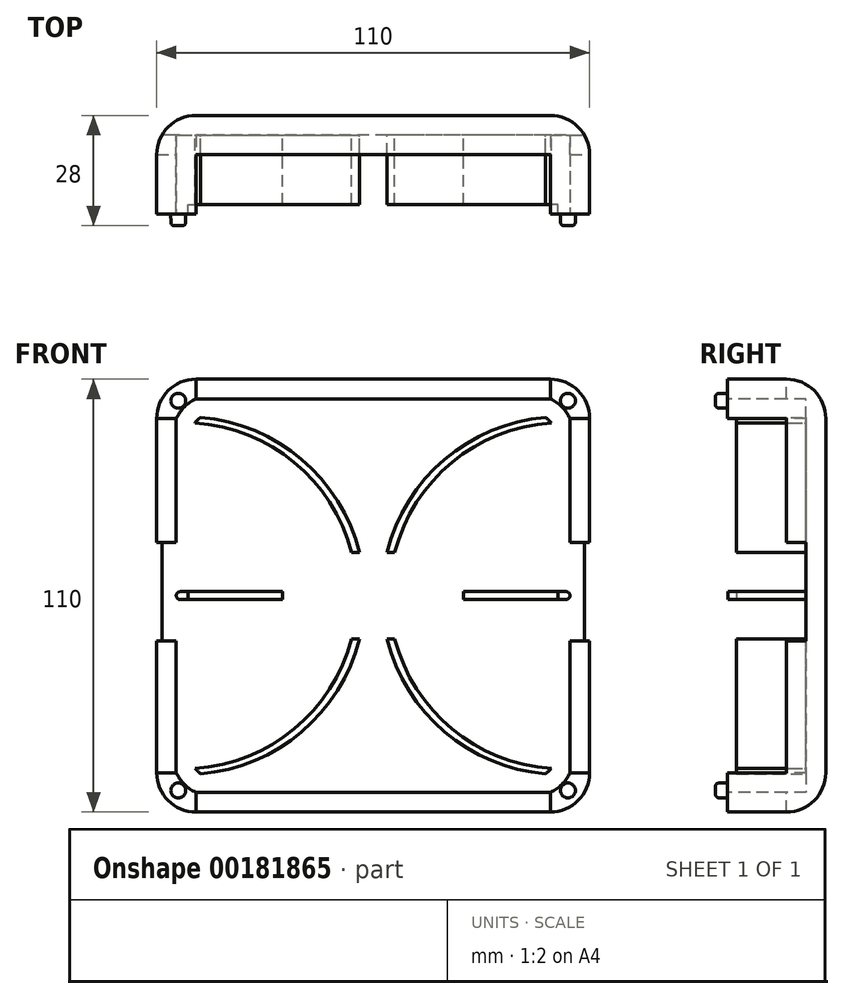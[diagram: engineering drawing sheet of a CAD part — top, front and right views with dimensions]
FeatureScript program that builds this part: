
annotation { "Feature Type Name" : "Feature", "Feature Type Description" : "" }
export const myFeature = defineFeature(function(context is Context, id is Id, definition is map)
    precondition{}
    {
        {
            var Q0;
            Q0=qCreatedBy(makeId("Front.planeOp"),FACE);
            var sketch = newSketch(context, id + "F0", { "sketchPlane" : qUnion([Q0])});
            skLineSegment(sketch, "E0.bottom", {"start": v(-55, 55) * mm, "end": v(55, 55) * mm});
            skLineSegment(sketch, "E0.top", {"start": v(-55, -55) * mm, "end": v(55, -55) * mm});
            skLineSegment(sketch, "E0.left", {"start": v(-55, 55) * mm, "end": v(-55, -55) * mm});
            skLineSegment(sketch, "E0.right", {"start": v(55, 55) * mm, "end": v(55, -55) * mm});
            skPoint(sketch, "E1", {"position": v(0, 55) * mm});
            skPoint(sketch, "E2", {"position": v(-55, 0) * mm});
            skPoint(sketch, "E3", {"position": v(55, 0) * mm});
            skPoint(sketch, "E4", {"position": v(0, -55) * mm});
            skSolve(sketch);
        }
        {
            var Q0;
            Q0=qSketchRegion(id+"F0",true);
            extrude(context, id + "F1", {"entities" : qUnion([Q0]), "endBound" : BoundingType.SYMMETRIC, "depth" : 50 * mm});
        }
        {
            var Q0;
            Q0=makeQuery(id+"F1.opExtrude","CAP_FACE",FACE,{"disambiguationData":[OSD([sQuery(id+"F0.wireOp",EDGE,"E0.bottom"),sQuery(id+"F0.wireOp",EDGE,"E0.top"),sQuery(id+"F0.wireOp",EDGE,"E0.left"),sQuery(id+"F0.wireOp",EDGE,"E0.right")])],"isStart":false});
            var Q1;
            Q1=makeQuery(id+"F1.opExtrude","SWEPT_FACE",FACE,{"disambiguationData":[OSD([sQuery(id+"F0.wireOp",EDGE,"E0.right")])]});
            var Q2;
            Q2=makeQuery(id+"F1.opExtrude","SWEPT_FACE",FACE,{"disambiguationData":[OSD([sQuery(id+"F0.wireOp",EDGE,"E0.bottom")])]});
            var Q3;
            Q3=makeQuery(id+"F1.opExtrude","SWEPT_FACE",FACE,{"disambiguationData":[OSD([sQuery(id+"F0.wireOp",EDGE,"E0.left")])]});
            var Q4;
            Q4=makeQuery(id+"F1.opExtrude","SWEPT_FACE",FACE,{"disambiguationData":[OSD([sQuery(id+"F0.wireOp",EDGE,"E0.top")])]});
            fillet(context, id + "F2", {"entities" : qUnion([Q0, Q1, Q2, Q3, Q4]), "radius" : 10 * mm, "allowEdgeOverflow" : false});
        }
        {
            var Q0;
            Q0=qCreatedBy(makeId("Front.planeOp"),FACE);
            var sketch = newSketch(context, id + "F3", { "sketchPlane" : qUnion([Q0])});
            skLineSegment(sketch, "E5.bottom", {"start": v(55, 55) * mm, "end": v(-55, 55) * mm});
            skLineSegment(sketch, "E5.top", {"start": v(55, -55) * mm, "end": v(-55, -55) * mm});
            skLineSegment(sketch, "E5.left", {"start": v(-55, 55) * mm, "end": v(-55, -55) * mm});
            skLineSegment(sketch, "E5.right", {"start": v(55, 55) * mm, "end": v(55, -55) * mm});
            skPoint(sketch, "E6", {"position": v(0, 55) * mm});
            skPoint(sketch, "E7", {"position": v(-55, 0) * mm});
            skPoint(sketch, "E8", {"position": v(55, 0) * mm});
            skPoint(sketch, "E9", {"position": v(0, -55) * mm});
            skSolve(sketch);
        }
        {
            var Q0;
            Q0=qSketchRegion(id+"F3",true);
            extrude(context, id + "F4", {"entities" : qUnion([Q0]), "operationType" : NewBodyOperationType.REMOVE, "depth" : 26 * mm});
        }
        {
            var Q0;
            Q0=qCreatedBy(makeId("Front.planeOp"),FACE);
            var sketch = newSketch(context, id + "F5", { "sketchPlane" : qUnion([Q0])});
            skLineSegment(sketch, "E10", {"start": v(45, 50) * mm, "end": v(-45, 50) * mm});
            skLineSegment(sketch, "E11", {"start": v(-45, 50) * mm, "end": v(-45, 45) * mm});
            skLineSegment(sketch, "E12", {"start": v(45, 50) * mm, "end": v(45, 45) * mm});
            skLineSegment(sketch, "E13", {"start": v(50, 45) * mm, "end": v(50, -45) * mm});
            skLineSegment(sketch, "E14", {"start": v(50, -45) * mm, "end": v(45, -45) * mm});
            skLineSegment(sketch, "E15", {"start": v(45, -45) * mm, "end": v(45, -50) * mm});
            skLineSegment(sketch, "E16", {"start": v(45, -50) * mm, "end": v(-45, -50) * mm});
            skLineSegment(sketch, "E17", {"start": v(-45, -50) * mm, "end": v(-45, -45) * mm});
            skLineSegment(sketch, "E18", {"start": v(-45, -45) * mm, "end": v(-50, -45) * mm});
            skLineSegment(sketch, "E19", {"start": v(-50, -45) * mm, "end": v(-50, 45) * mm});
            skLineSegment(sketch, "E20", {"start": v(-50, 45) * mm, "end": v(-45, 45) * mm});
            skLineSegment(sketch, "E21.MirrorCS", {"start": v(50, 45) * mm, "end": v(45, 45) * mm});
            skSolve(sketch);
        }
        {
            var Q0;
            Q0=qSketchRegion(id+"F5",true);
            extrude(context, id + "F6", {"entities" : qUnion([Q0]), "operationType" : NewBodyOperationType.REMOVE, "oppositeDirection" : true, "depth" : 20 * mm});
        }
        {
            var Q0;
            Q0=makeQuery(id+"F4.boolean.opBoolean","COPY",FACE,{"derivedFrom":makeQuery(id+"F4.opExtrude","CAP_FACE",FACE,{"disambiguationData":[OSD([sQuery(id+"F3.wireOp",EDGE,"E5.bottom"),sQuery(id+"F3.wireOp",EDGE,"E5.top"),sQuery(id+"F3.wireOp",EDGE,"E5.left"),sQuery(id+"F3.wireOp",EDGE,"E5.right")])],"isStart":true})});
            var sketch = newSketch(context, id + "F7", { "sketchPlane" : qUnion([Q0])});
            skCircle(sketch, "E22", {"center": v(49.5, 49.5) * mm, "radius": 1.9 * mm});
            skCircle(sketch, "E23.MirrorC", {"center": v(-49.5, 49.5) * mm, "radius": 1.9 * mm});
            skCircle(sketch, "E24.MirrorC", {"center": v(49.5, -49.5) * mm, "radius": 1.9 * mm});
            skCircle(sketch, "E25.MirrorC", {"center": v(-49.5, -49.5) * mm, "radius": 1.9 * mm});
            skSolve(sketch);
        }
        {
            var Q0;
            Q0=qSketchRegion(id+"F7",true);
            extrude(context, id + "F8", {"entities" : qUnion([Q0]), "operationType" : NewBodyOperationType.ADD, "depth" : 3 * mm, "hasDraft" : true, "draftAngle" : 1 * degree, "draftPullDirection" : true});
        }
        {
            var Q0;
            Q0=makeQuery(id+"F4.boolean.opBoolean","COPY",FACE,{"derivedFrom":makeQuery(id+"F4.opExtrude","CAP_FACE",FACE,{"disambiguationData":[OSD([sQuery(id+"F3.wireOp",EDGE,"E5.bottom"),sQuery(id+"F3.wireOp",EDGE,"E5.top"),sQuery(id+"F3.wireOp",EDGE,"E5.left"),sQuery(id+"F3.wireOp",EDGE,"E5.right")])],"isStart":true})});
            var sketch = newSketch(context, id + "F9", { "sketchPlane" : qUnion([Q0])});
            skArc(sketch, "E26", {"start": v(-45, 50) * mm, "mid": v(-47.96, 47.96) * mm, "end": v(-50, 45) * mm});
            skLineSegment(sketch, "E27", {"start": v(-45, 50) * mm, "end": v(-45, 45) * mm});
            skLineSegment(sketch, "E28", {"start": v(-45, 45) * mm, "end": v(-50, 45) * mm});
            skLineSegment(sketch, "E29.MirrorCS", {"start": v(-45, -50) * mm, "end": v(-45, -45) * mm});
            skArc(sketch, "E30.MirrorCS", {"start": v(-45, -50) * mm, "mid": v(-47.96, -47.96) * mm, "end": v(-50, -45) * mm});
            skLineSegment(sketch, "E31.MirrorCS", {"start": v(-45, -45) * mm, "end": v(-50, -45) * mm});
            skArc(sketch, "E32.MirrorCS", {"start": v(45, 50) * mm, "mid": v(47.96, 47.96) * mm, "end": v(50, 45) * mm});
            skLineSegment(sketch, "E33.MirrorCS", {"start": v(45, 50) * mm, "end": v(45, 45) * mm});
            skLineSegment(sketch, "E34.MirrorCS", {"start": v(45, 45) * mm, "end": v(50, 45) * mm});
            skLineSegment(sketch, "E35.MirrorCS", {"start": v(45, -45) * mm, "end": v(50, -45) * mm});
            skArc(sketch, "E36.MirrorCS", {"start": v(45, -50) * mm, "mid": v(47.96, -47.96) * mm, "end": v(50, -45) * mm});
            skLineSegment(sketch, "E37.MirrorCS", {"start": v(45, -50) * mm, "end": v(45, -45) * mm});
            skSolve(sketch);
        }
        {
            var Q0;
            Q0 = qSketchRegion(id + "F9", true);
            extrude(context, id + "F10", {"entities" : qUnion([Q0]), "operationType" : NewBodyOperationType.REMOVE, "oppositeDirection" : true, "depth" : 20 * mm});
        }
        {
            var Q0;
            Q0=makeQuery(id+"F1.opExtrude","SWEPT_FACE",FACE,{"disambiguationData":[OSD([sQuery(id+"F0.wireOp",EDGE,"E0.bottom")])]});
            var sketch = newSketch(context, id + "F11", { "sketchPlane" : qUnion([Q0])});
            skLineSegment(sketch, "E38.bottom", {"start": v(-45, 15) * mm, "end": v(45, 15) * mm});
            skLineSegment(sketch, "E38.top", {"start": v(-45, 0) * mm, "end": v(45, 0) * mm});
            skLineSegment(sketch, "E38.left", {"start": v(-45, 15) * mm, "end": v(-45, 0) * mm});
            skLineSegment(sketch, "E38.right", {"start": v(45, 15) * mm, "end": v(45, 0) * mm});
            skSolve(sketch);
        }
        {
            var Q0;
            Q0 = qSketchRegion(id + "F11", true);
            extrude(context, id + "F12", {"entities" : qUnion([Q0]), "operationType" : NewBodyOperationType.REMOVE, "oppositeDirection" : true, "depth" : 110 * mm});
        }
        {
            var Q0;
            Q0=makeQuery(id+"F1.opExtrude","SWEPT_FACE",FACE,{"disambiguationData":[OSD([sQuery(id+"F0.wireOp",EDGE,"E0.left")])]});
            var sketch = newSketch(context, id + "F13", { "sketchPlane" : qUnion([Q0])});
            skLineSegment(sketch, "E39.bottom", {"start": v(-15, -45) * mm, "end": v(0, -45) * mm});
            skLineSegment(sketch, "E39.top", {"start": v(-15, 45) * mm, "end": v(0, 45) * mm});
            skLineSegment(sketch, "E39.left", {"start": v(-15, -45) * mm, "end": v(-15, 45) * mm});
            skLineSegment(sketch, "E39.right", {"start": v(0, -45) * mm, "end": v(0, 45) * mm});
            skSolve(sketch);
        }
        {
            var Q0;
            Q0 = qSketchRegion(id + "F13", true);
            extrude(context, id + "F14", {"entities" : qUnion([Q0]), "operationType" : NewBodyOperationType.REMOVE, "oppositeDirection" : true, "depth" : 110 * mm});
        }
        {
            var Q0;
            Q0=makeQuery(id+"F10.boolean.opBoolean","MERGE",FACE,{"derivedFrom":[makeQuery(id+"F6.boolean.opBoolean","COPY",FACE,{"derivedFrom":makeQuery(id+"F6.opExtrude","CAP_FACE",FACE,{"disambiguationData":[OSD([sQuery(id+"F5.wireOp",EDGE,"E10"),sQuery(id+"F5.wireOp",EDGE,"E11"),sQuery(id+"F5.wireOp",EDGE,"E12"),sQuery(id+"F5.wireOp",EDGE,"Rgk4YyDA-dK0y-lxdy-LCG8-8X0n81pjpPL2"),sQuery(id+"F5.wireOp",EDGE,"E13"),sQuery(id+"F5.wireOp",EDGE,"E14"),sQuery(id+"F5.wireOp",EDGE,"E15"),sQuery(id+"F5.wireOp",EDGE,"E16"),sQuery(id+"F5.wireOp",EDGE,"E17"),sQuery(id+"F5.wireOp",EDGE,"E18"),sQuery(id+"F5.wireOp",EDGE,"E19"),sQuery(id+"F5.wireOp",EDGE,"E20")])],"isStart":false})}),makeQuery(id+"F10.opExtrude","CAP_FACE",FACE,{"disambiguationData":[OSD([sQuery(id+"F9.wireOp",EDGE,"E26"),sQuery(id+"F9.wireOp",EDGE,"E27"),sQuery(id+"F9.wireOp",EDGE,"E28")])],"isStart":false}),makeQuery(id+"F10.opExtrude","CAP_FACE",FACE,{"disambiguationData":[OSD([sQuery(id+"F9.wireOp",EDGE,"E29.MirrorCS"),sQuery(id+"F9.wireOp",EDGE,"E30.MirrorCS"),sQuery(id+"F9.wireOp",EDGE,"E31.MirrorCS")])],"isStart":false}),makeQuery(id+"F10.opExtrude","CAP_FACE",FACE,{"disambiguationData":[OSD([sQuery(id+"F9.wireOp",EDGE,"713af9eb-3523-4645-b4d6-e8278202f2d70.MirrorCS"),sQuery(id+"F9.wireOp",EDGE,"aa040882-3397-4691-b8a4-aef4612770bb0.MirrorCS"),sQuery(id+"F9.wireOp",EDGE,"7d541f15-c5d7-4458-aec9-df448ef9912d0.MirrorCS")])],"isStart":false}),makeQuery(id+"F10.opExtrude","CAP_FACE",FACE,{"disambiguationData":[OSD([sQuery(id+"F9.wireOp",EDGE,"zS62jr0F-Xqa5-w36F-4dhE-6Vk6gu5LrxYo"),sQuery(id+"F9.wireOp",EDGE,"QpDyHDuu-1PBp-T7AA-cmtf-nKKC5eDHPDcg"),sQuery(id+"F9.wireOp",EDGE,"hVT4Xi0K-uElt-0SsE-6UHd-I7Wh2zfzxc4D")])],"isStart":false})]});
            var sketch = newSketch(context, id + "F15", { "sketchPlane" : qUnion([Q0])});
            skLineSegment(sketch, "E40.bottom", {"start": v(-50, 1) * mm, "end": v(-23, 1) * mm});
            skLineSegment(sketch, "E40.top", {"start": v(-50, -1) * mm, "end": v(-23, -1) * mm});
            skLineSegment(sketch, "E40.left", {"start": v(-50, 1) * mm, "end": v(-50, -1) * mm});
            skLineSegment(sketch, "E40.right", {"start": v(-23, 1) * mm, "end": v(-23, -1) * mm});
            skPoint(sketch, "E41", {"position": v(-50, 0) * mm});
            skLineSegment(sketch, "E42.MirrorCS", {"start": v(50, 1) * mm, "end": v(23, 1) * mm});
            skLineSegment(sketch, "E43.MirrorCS", {"start": v(50, -1) * mm, "end": v(23, -1) * mm});
            skLineSegment(sketch, "E44.MirrorCS", {"start": v(23, 1) * mm, "end": v(23, -1) * mm});
            skLineSegment(sketch, "E45.MirrorCS", {"start": v(50, 1) * mm, "end": v(50, -1) * mm});
            skLineSegment(sketch, "E46.bottom", {"start": v(-23, 8) * mm, "end": v(23, 8) * mm});
            skLineSegment(sketch, "E46.top", {"start": v(-23, -8) * mm, "end": v(23, -8) * mm});
            skPoint(sketch, "E47", {"position": v(-23, 0) * mm});
            skPoint(sketch, "E48", {"position": v(0, 8) * mm});
            skPoint(sketch, "E49", {"position": v(-3.5, 8) * mm});
            skArc(sketch, "E50", {"start": v(-3.5, 11) * mm, "mid": v(-18.17, 34.62) * mm, "end": v(-43.85, 45.26) * mm});
            skPoint(sketch, "E51", {"position": v(-43.85, 45.26) * mm});
            skPoint(sketch, "E52", {"position": v(-45.26, 43.85) * mm});
            skPoint(sketch, "E53", {"position": v(-5.5, 8) * mm});
            skArc(sketch, "E54", {"start": v(-5.5, 11) * mm, "mid": v(-20.05, 33.87) * mm, "end": v(-45.26, 43.85) * mm});
            skLineSegment(sketch, "E55", {"start": v(-5.5, 11) * mm, "end": v(-3.5, 11) * mm});
            skArc(sketch, "E56", {"start": v(-43.85, 45.26) * mm, "mid": v(-44.6, 44.6) * mm, "end": v(-45.26, 43.85) * mm});
            skArc(sketch, "E57.MirrorCS", {"start": v(5.5, 11) * mm, "mid": v(20.05, 33.87) * mm, "end": v(45.26, 43.85) * mm});
            skArc(sketch, "E58.MirrorCS", {"start": v(3.5, 11) * mm, "mid": v(18.17, 34.62) * mm, "end": v(43.85, 45.26) * mm});
            skArc(sketch, "E59.MirrorCS", {"start": v(43.85, 45.26) * mm, "mid": v(44.6, 44.6) * mm, "end": v(45.26, 43.85) * mm});
            skLineSegment(sketch, "E60.MirrorCS", {"start": v(5.5, 11) * mm, "end": v(3.5, 11) * mm});
            skArc(sketch, "E61.MirrorCS", {"start": v(-5.5, -11) * mm, "mid": v(-20.05, -33.87) * mm, "end": v(-45.26, -43.85) * mm});
            skArc(sketch, "E62.MirrorCS", {"start": v(-3.5, -11) * mm, "mid": v(-18.17, -34.62) * mm, "end": v(-43.85, -45.26) * mm});
            skArc(sketch, "E63.MirrorCS", {"start": v(5.5, -11) * mm, "mid": v(20.05, -33.87) * mm, "end": v(45.26, -43.85) * mm});
            skArc(sketch, "E64.MirrorCS", {"start": v(3.5, -11) * mm, "mid": v(18.17, -34.62) * mm, "end": v(43.85, -45.26) * mm});
            skLineSegment(sketch, "E65.MirrorCS", {"start": v(-5.5, -11) * mm, "end": v(-3.5, -11) * mm});
            skLineSegment(sketch, "E66.MirrorCS", {"start": v(5.5, -11) * mm, "end": v(3.5, -11) * mm});
            skArc(sketch, "E67.MirrorCS", {"start": v(43.85, -45.26) * mm, "mid": v(44.6, -44.6) * mm, "end": v(45.26, -43.85) * mm});
            skArc(sketch, "E68.MirrorCS", {"start": v(-43.85, -45.26) * mm, "mid": v(-44.6, -44.6) * mm, "end": v(-45.26, -43.85) * mm});
            skSolve(sketch);
        }
        {
            var Q0;
            Q0 = qSketchRegion(id + "F15", true);
            extrude(context, id + "F16", {"entities" : qUnion([Q0]), "operationType" : NewBodyOperationType.ADD, "depth" : 17.7 * mm});
        }
        {
            var Q0;
            Q0=makeQuery(id+"F16.opExtrude","SWEPT_FACE",FACE,{"disambiguationData":[OSD([sQuery(id+"F15.wireOp",EDGE,"E42.MirrorCS")])]});
            var sketch = newSketch(context, id + "F17", { "sketchPlane" : qUnion([Q0])});
            skArc(sketch, "E69", {"start": v(50, 6.34) * mm, "mid": v(54.66, 17.59) * mm, "end": v(45, 25) * mm});
            skLineSegment(sketch, "E70", {"start": v(50, 20) * mm, "end": v(53.66, 20) * mm});
            skLineSegment(sketch, "E71", {"start": v(50, 20) * mm, "end": v(50, 6.34) * mm});
            skArc(sketch, "E72.MirrorCS", {"start": v(-50, 6.34) * mm, "mid": v(-54.66, 17.59) * mm, "end": v(-45, 25) * mm});
            skLineSegment(sketch, "E73.MirrorCS", {"start": v(-50, 20) * mm, "end": v(-53.66, 20) * mm});
            skLineSegment(sketch, "E74.MirrorCS", {"start": v(-50, 20) * mm, "end": v(-50, 6.34) * mm});
            skSolve(sketch);
        }
        {
            var Q0;
            Q0 = qSketchRegion(id + "F17", true);
            extrude(context, id + "F18", {"entities" : qUnion([Q0]), "operationType" : NewBodyOperationType.REMOVE, "endBound" : BoundingType.SYMMETRIC, "oppositeDirection" : true, "depth" : 25 * mm});
        }
        {
            var Q0;
            Q0=makeQuery(id+"F16.opExtrude","CAP_FACE",FACE,{"disambiguationData":[OSD([sQuery(id+"F15.wireOp",EDGE,"E40.bottom"),sQuery(id+"F15.wireOp",EDGE,"E40.top"),sQuery(id+"F15.wireOp",EDGE,"E40.left"),sQuery(id+"F15.wireOp",EDGE,"E40.right")])],"isStart":false});
            var sketch = newSketch(context, id + "F19", { "sketchPlane" : qUnion([Q0])});
            skLineSegment(sketch, "E75.bottom", {"start": v(-50, 1) * mm, "end": v(-47, 1) * mm});
            skLineSegment(sketch, "E75.top", {"start": v(-50, -1) * mm, "end": v(-47, -1) * mm});
            skLineSegment(sketch, "E75.left", {"start": v(-50, 1) * mm, "end": v(-50, -1) * mm});
            skLineSegment(sketch, "E75.right", {"start": v(-47, 1) * mm, "end": v(-47, -1) * mm});
            skLineSegment(sketch, "E76.MirrorCS", {"start": v(50, 1) * mm, "end": v(47, 1) * mm});
            skLineSegment(sketch, "E77.MirrorCS", {"start": v(50, 1) * mm, "end": v(50, -1) * mm});
            skLineSegment(sketch, "E78.MirrorCS", {"start": v(50, -1) * mm, "end": v(47, -1) * mm});
            skLineSegment(sketch, "E79.MirrorCS", {"start": v(47, 1) * mm, "end": v(47, -1) * mm});
            skSolve(sketch);
        }
        {
            var Q0;
            Q0 = qSketchRegion(id + "F19", true);
            extrude(context, id + "F20", {"entities" : qUnion([Q0]), "operationType" : NewBodyOperationType.ADD, "depth" : 2.2 * mm});
        }
        {
            var Q0;
            {var subQ0=sQuery(id+"F15.wireOp",EDGE,"E45.MirrorCS");var subQ1=sQuery(id+"F15.wireOp",EDGE,"E42.MirrorCS");Q0=makeQuery(id+"F20.boolean.opBoolean","MERGE",EDGE,{"derivedFrom":[makeQuery(id+"F16.boolean.opBoolean","SPLIT",EDGE,{"disambiguationData":[TD([makeQuery(id+"F16.opExtrude","CAP_FACE",FACE,{"disambiguationData":[OSD([subQ1,sQuery(id+"F15.wireOp",EDGE,"E43.MirrorCS"),sQuery(id+"F15.wireOp",EDGE,"E44.MirrorCS"),subQ0])],"isStart":false})])],"derivedFrom":makeQuery(id+"F16.opExtrude","SWEPT_EDGE",EDGE,{"disambiguationData":[OSD([subQ1,subQ0])]})}),makeQuery(id+"F20.opExtrude","SWEPT_EDGE",EDGE,{"disambiguationData":[OSD([sQuery(id+"F19.wireOp",EDGE,"E76.MirrorCS"),sQuery(id+"F19.wireOp",EDGE,"E77.MirrorCS")])]})]});}
            var Q1;
            {var subQ0=sQuery(id+"F15.wireOp",EDGE,"E43.MirrorCS");var subQ1=sQuery(id+"F15.wireOp",EDGE,"E45.MirrorCS");Q1=makeQuery(id+"F20.boolean.opBoolean","MERGE",EDGE,{"derivedFrom":[makeQuery(id+"F16.boolean.opBoolean","SPLIT",EDGE,{"disambiguationData":[TD([makeQuery(id+"F16.opExtrude","CAP_FACE",FACE,{"disambiguationData":[OSD([sQuery(id+"F15.wireOp",EDGE,"E42.MirrorCS"),subQ0,sQuery(id+"F15.wireOp",EDGE,"E44.MirrorCS"),subQ1])],"isStart":false})])],"derivedFrom":makeQuery(id+"F16.opExtrude","SWEPT_EDGE",EDGE,{"disambiguationData":[OSD([subQ0,subQ1])]})}),makeQuery(id+"F20.opExtrude","SWEPT_EDGE",EDGE,{"disambiguationData":[OSD([sQuery(id+"F19.wireOp",EDGE,"E77.MirrorCS"),sQuery(id+"F19.wireOp",EDGE,"E78.MirrorCS")])]})]});}
            var Q2;
            {var subQ0=sQuery(id+"F15.wireOp",EDGE,"E40.left");var subQ1=sQuery(id+"F15.wireOp",EDGE,"E40.bottom");Q2=makeQuery(id+"F20.boolean.opBoolean","MERGE",EDGE,{"derivedFrom":[makeQuery(id+"F16.boolean.opBoolean","SPLIT",EDGE,{"disambiguationData":[TD([makeQuery(id+"F16.opExtrude","CAP_FACE",FACE,{"disambiguationData":[OSD([subQ1,sQuery(id+"F15.wireOp",EDGE,"E40.top"),subQ0,sQuery(id+"F15.wireOp",EDGE,"E40.right")])],"isStart":false})])],"derivedFrom":makeQuery(id+"F16.opExtrude","SWEPT_EDGE",EDGE,{"disambiguationData":[OSD([subQ1,subQ0])]})}),makeQuery(id+"F20.opExtrude","SWEPT_EDGE",EDGE,{"disambiguationData":[OSD([sQuery(id+"F19.wireOp",EDGE,"E75.bottom"),sQuery(id+"F19.wireOp",EDGE,"E75.left")])]})]});}
            var Q3;
            {var subQ0=sQuery(id+"F15.wireOp",EDGE,"E40.top");var subQ1=sQuery(id+"F15.wireOp",EDGE,"E40.left");Q3=makeQuery(id+"F20.boolean.opBoolean","MERGE",EDGE,{"derivedFrom":[makeQuery(id+"F16.boolean.opBoolean","SPLIT",EDGE,{"disambiguationData":[TD([makeQuery(id+"F16.opExtrude","CAP_FACE",FACE,{"disambiguationData":[OSD([sQuery(id+"F15.wireOp",EDGE,"E40.bottom"),subQ0,subQ1,sQuery(id+"F15.wireOp",EDGE,"E40.right")])],"isStart":false})])],"derivedFrom":makeQuery(id+"F16.opExtrude","SWEPT_EDGE",EDGE,{"disambiguationData":[OSD([subQ0,subQ1])]})}),makeQuery(id+"F20.opExtrude","SWEPT_EDGE",EDGE,{"disambiguationData":[OSD([sQuery(id+"F19.wireOp",EDGE,"E75.top"),sQuery(id+"F19.wireOp",EDGE,"E75.left")])]})]});}
            fillet(context, id + "F21", {"entities" : qUnion([Q0, Q1, Q2, Q3]), "radius" : 1 * mm, "tangentPropagation" : true, "allowEdgeOverflow" : false});
        }
        {
            var Q0;
            Q0=makeQuery(id+"F8.opExtrude","CAP_EDGE",EDGE,{"disambiguationData":[OSD([sQuery(id+"F7.wireOp",EDGE,"E23.MirrorC")])],"isStart":false});
            var Q1;
            Q1=makeQuery(id+"F8.opExtrude","CAP_EDGE",EDGE,{"disambiguationData":[OSD([sQuery(id+"F7.wireOp",EDGE,"E22")])],"isStart":false});
            var Q2;
            Q2=makeQuery(id+"F8.opExtrude","CAP_EDGE",EDGE,{"disambiguationData":[OSD([sQuery(id+"F7.wireOp",EDGE,"E24.MirrorC")])],"isStart":false});
            var Q3;
            Q3=makeQuery(id+"F8.opExtrude","CAP_EDGE",EDGE,{"disambiguationData":[OSD([sQuery(id+"F7.wireOp",EDGE,"E25.MirrorC")])],"isStart":false});
            fillet(context, id + "F22", {"entities" : qUnion([Q0, Q1, Q2, Q3]), "radius" : 0.8 * mm, "tangentPropagation" : true, "allowEdgeOverflow" : false});
        }
    });
